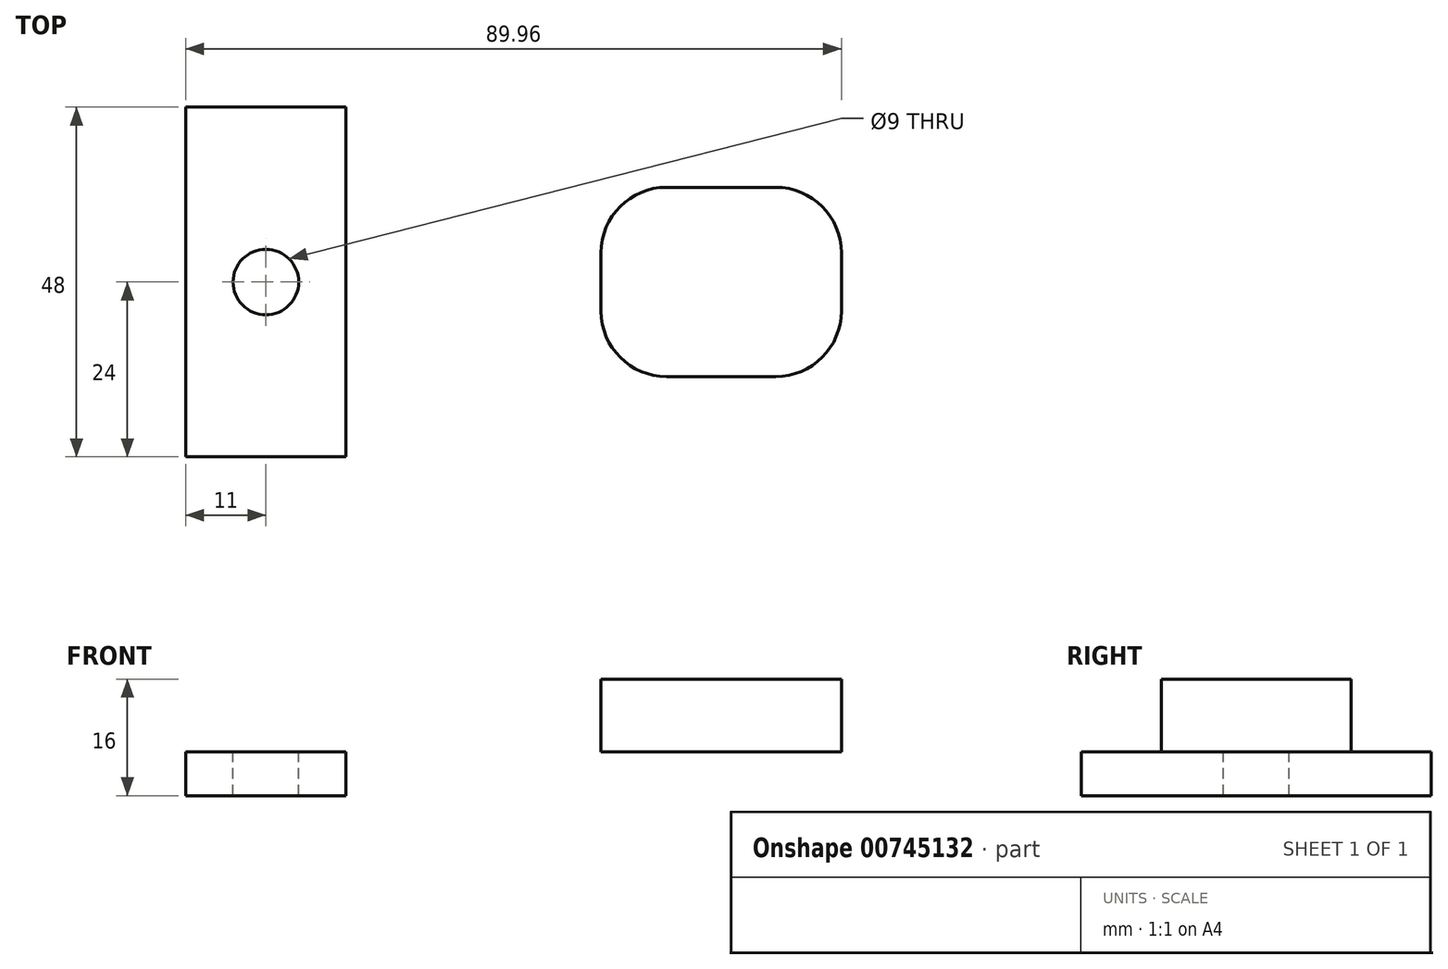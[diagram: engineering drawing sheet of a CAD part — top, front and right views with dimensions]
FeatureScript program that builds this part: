
annotation { "Feature Type Name" : "Feature", "Feature Type Description" : "" }
export const myFeature = defineFeature(function(context is Context, id is Id, definition is map)
    precondition{}
    {
        {
            var Q0;
            Q0=qCreatedBy(makeId("Front.planeOp"),FACE);
            var sketch = newSketch(context, id + "F0", { "sketchPlane" : qUnion([Q0])});
            skLineSegment(sketch, "E0", {"start": v(-11, 0) * mm, "end": v(-11, -6) * mm});
            skLineSegment(sketch, "E1", {"start": v(-11, -6) * mm, "end": v(11, -6) * mm});
            skLineSegment(sketch, "E2", {"start": v(11, -6) * mm, "end": v(11, 0) * mm});
            skLineSegment(sketch, "E3", {"start": v(11, 0) * mm, "end": v(100, 0) * mm});
            skLineSegment(sketch, "E4", {"start": v(100, 0) * mm, "end": v(100, 10) * mm});
            skLineSegment(sketch, "E5", {"start": v(100, 10) * mm, "end": v(-100, 10) * mm});
            skLineSegment(sketch, "E6", {"start": v(-100, 10) * mm, "end": v(-100, 0) * mm});
            skLineSegment(sketch, "E7", {"start": v(-100, 0) * mm, "end": v(-11, 0) * mm});
            skSolve(sketch);
        }
        {
            var Q0;
            Q0 = qSketchRegion(id + "F0", true);
            extrude(context, id + "F1", {"entities" : qUnion([Q0]), "depth" : 48 * mm, "offsetDistance" : 25 * mm});
        }
        {
            var Q0;
            Q0=makeQuery(id+"F1.opExtrude","SWEPT_FACE",FACE,{"disambiguationData":[OSD([sQuery(id+"F0.wireOp",EDGE,"E5")])]});
            var sketch = newSketch(context, id + "F2", { "sketchPlane" : qUnion([Q0])});
            skArc(sketch, "E8", {"start": v(-78.96, -27.99) * mm, "mid": v(-76.33, -34.35) * mm, "end": v(-69.96, -36.98) * mm});
            skLineSegment(sketch, "E9", {"start": v(-78.96, -19.99) * mm, "end": v(-78.96, -27.99) * mm});
            skLineSegment(sketch, "E10", {"start": v(-69.96, -11) * mm, "end": v(-54.97, -11) * mm});
            skLineSegment(sketch, "E11", {"start": v(-45.98, -19.99) * mm, "end": v(-45.98, -27.99) * mm});
            skLineSegment(sketch, "E12", {"start": v(-69.96, -36.98) * mm, "end": v(-54.97, -36.98) * mm});
            skArc(sketch, "E13.trimOffspring", {"start": v(-69.96, -11) * mm, "mid": v(-76.33, -13.63) * mm, "end": v(-78.96, -19.99) * mm});
            skArc(sketch, "E14.trimOffspring", {"start": v(-45.98, -19.99) * mm, "mid": v(-48.61, -13.63) * mm, "end": v(-54.97, -11) * mm});
            skArc(sketch, "E15.trimOffspring", {"start": v(-54.97, -36.98) * mm, "mid": v(-48.61, -34.35) * mm, "end": v(-45.98, -27.99) * mm});
            skArc(sketch, "E16.MirrorCS", {"start": v(54.97, -36.98) * mm, "mid": v(48.61, -34.35) * mm, "end": v(45.98, -27.99) * mm});
            skArc(sketch, "E17.MirrorCS", {"start": v(78.96, -27.99) * mm, "mid": v(76.33, -34.35) * mm, "end": v(69.96, -36.98) * mm});
            skArc(sketch, "E18.MirrorCS", {"start": v(69.96, -11) * mm, "mid": v(76.33, -13.63) * mm, "end": v(78.96, -19.99) * mm});
            skLineSegment(sketch, "E19.MirrorCS", {"start": v(69.96, -36.98) * mm, "end": v(54.97, -36.98) * mm});
            skLineSegment(sketch, "E20.MirrorCS", {"start": v(78.96, -19.99) * mm, "end": v(78.96, -27.99) * mm});
            skArc(sketch, "E21.MirrorCS", {"start": v(45.98, -19.99) * mm, "mid": v(48.61, -13.63) * mm, "end": v(54.97, -11) * mm});
            skLineSegment(sketch, "E22.MirrorCS", {"start": v(69.96, -11) * mm, "end": v(54.97, -11) * mm});
            skLineSegment(sketch, "E23.MirrorCS", {"start": v(45.98, -19.99) * mm, "end": v(45.98, -27.99) * mm});
            skCircle(sketch, "E24", {"center": v(0, -24) * mm, "radius": 7 * mm});
            skCircle(sketch, "E25", {"center": v(0, -24) * mm, "radius": 4.5 * mm});
            skSolve(sketch);
        }
        {
            var Q0;
            Q0=makeQuery(id+"F2.imprint","IMPRINT",FACE,{"disambiguationData":[TD([[makeQuery(id+"F2.imprint","IMPRINT",EDGE,{"derivedFrom":sQuery(id+"F2.wireOp",EDGE,"E8")}),1.0]])]});
            var Q1;
            Q1=makeQuery(id+"F2.imprint","IMPRINT",FACE,{"disambiguationData":[TD([[makeQuery(id+"F2.imprint","IMPRINT",EDGE,{"derivedFrom":sQuery(id+"F2.wireOp",EDGE,"E16.MirrorCS")}),-1.0]])]});
            extrude(context, id + "F3", {"entities" : qUnion([Q0, Q1]), "operationType" : NewBodyOperationType.REMOVE, "oppositeDirection" : true, "depth" : 10 * mm, "offsetDistance" : 25 * mm});
        }
        {
            var Q0;
            Q0=makeQuery(id+"F2.imprint","IMPRINT",FACE,{"disambiguationData":[TD([[makeQuery(id+"F2.imprint","IMPRINT",EDGE,{"derivedFrom":sQuery(id+"F2.wireOp",EDGE,"E24")}),1.0]])]});
            extrude(context, id + "F4", {"entities" : qUnion([Q0]), "operationType" : NewBodyOperationType.REMOVE, "oppositeDirection" : true, "depth" : 10 * mm, "offsetDistance" : 25 * mm});
        }
        {
            var Q0;
            Q0=makeQuery(id+"F2.imprint","IMPRINT",FACE,{"disambiguationData":[TD([[makeQuery(id+"F2.imprint","IMPRINT",EDGE,{"derivedFrom":sQuery(id+"F2.wireOp",EDGE,"E25")}),1.0]])]});
            extrude(context, id + "F5", {"entities" : qUnion([Q0]), "operationType" : NewBodyOperationType.REMOVE, "oppositeDirection" : true, "depth" : 25 * mm, "offsetDistance" : 25 * mm});
        }
    });
